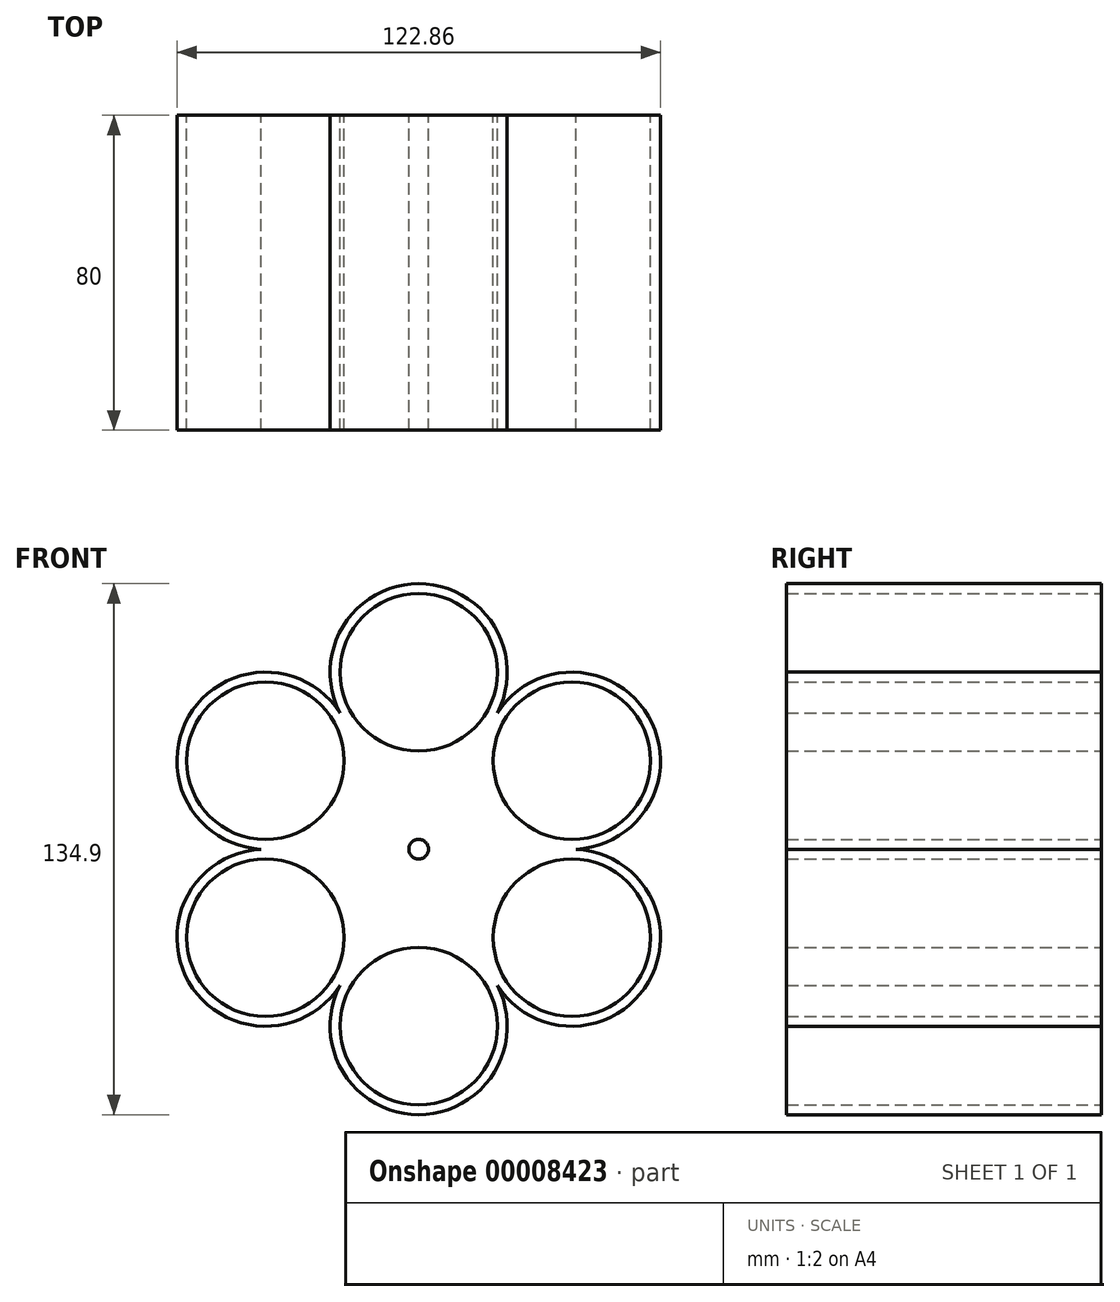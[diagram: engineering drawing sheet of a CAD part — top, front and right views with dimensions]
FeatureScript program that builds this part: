
annotation { "Feature Type Name" : "Feature", "Feature Type Description" : "" }
export const myFeature = defineFeature(function(context is Context, id is Id, definition is map)
    precondition{}
    {
        {
            var Q0;
            Q0=qCreatedBy(makeId("Front.planeOp"),FACE);
            var sketch = newSketch(context, id + "F0", { "sketchPlane" : qUnion([Q0])});
            skCircle(sketch, "E0.cCircle", {"center": v(0, 0) * mm, "radius": 34.64 * mm, "construction": true});
            skLineSegment(sketch, "E0.0", {"start": v(-20, 34.64) * mm, "end": v(20, 34.64) * mm});
            skLineSegment(sketch, "E0.1", {"start": v(20, 34.64) * mm, "end": v(40, 0) * mm});
            skLineSegment(sketch, "E0.2", {"start": v(40, 0) * mm, "end": v(20, -34.64) * mm});
            skLineSegment(sketch, "E0.3", {"start": v(20, -34.64) * mm, "end": v(-20, -34.64) * mm});
            skLineSegment(sketch, "E0.4", {"start": v(-20, -34.64) * mm, "end": v(-40, 0) * mm});
            skLineSegment(sketch, "E0.5", {"start": v(-40, 0) * mm, "end": v(-20, 34.64) * mm});
            skPoint(sketch, "E0.0.midPoint", {"position": v(0, 34.64) * mm});
            skArc(sketch, "E1", {"start": v(20, 34.64) * mm, "mid": v(0, 67.45) * mm, "end": v(-20, 34.64) * mm});
            skArc(sketch, "E2", {"start": v(40, 0) * mm, "mid": v(58.41, 33.72) * mm, "end": v(20, 34.64) * mm});
            skArc(sketch, "E3", {"start": v(20, -34.64) * mm, "mid": v(58.41, -33.72) * mm, "end": v(40, 0) * mm});
            skArc(sketch, "E4", {"start": v(-20, -34.64) * mm, "mid": v(0, -67.45) * mm, "end": v(20, -34.64) * mm});
            skArc(sketch, "E5", {"start": v(-40, 0) * mm, "mid": v(-58.41, -33.72) * mm, "end": v(-20, -34.64) * mm});
            skArc(sketch, "E6", {"start": v(-20, 34.64) * mm, "mid": v(-58.41, 33.72) * mm, "end": v(-40, 0) * mm});
            skCircle(sketch, "E7", {"center": v(-38.93, 22.47) * mm, "radius": 20 * mm});
            skCircle(sketch, "E8", {"center": v(0, 44.95) * mm, "radius": 20 * mm});
            skCircle(sketch, "E9", {"center": v(38.93, 22.47) * mm, "radius": 20 * mm});
            skCircle(sketch, "E10", {"center": v(38.93, -22.47) * mm, "radius": 20 * mm});
            skCircle(sketch, "E11", {"center": v(0, -44.95) * mm, "radius": 20 * mm});
            skCircle(sketch, "E12", {"center": v(-38.93, -22.47) * mm, "radius": 20 * mm});
            skCircle(sketch, "E13", {"center": v(0, 0) * mm, "radius": 2.5 * mm});
            skSolve(sketch);
        }
        {
            var Q0;
            Q0 = qSketchRegion(id + "F0", true);
            extrude(context, id + "F1", {"entities" : qUnion([Q0]), "depth" : 80 * mm});
        }
    });
